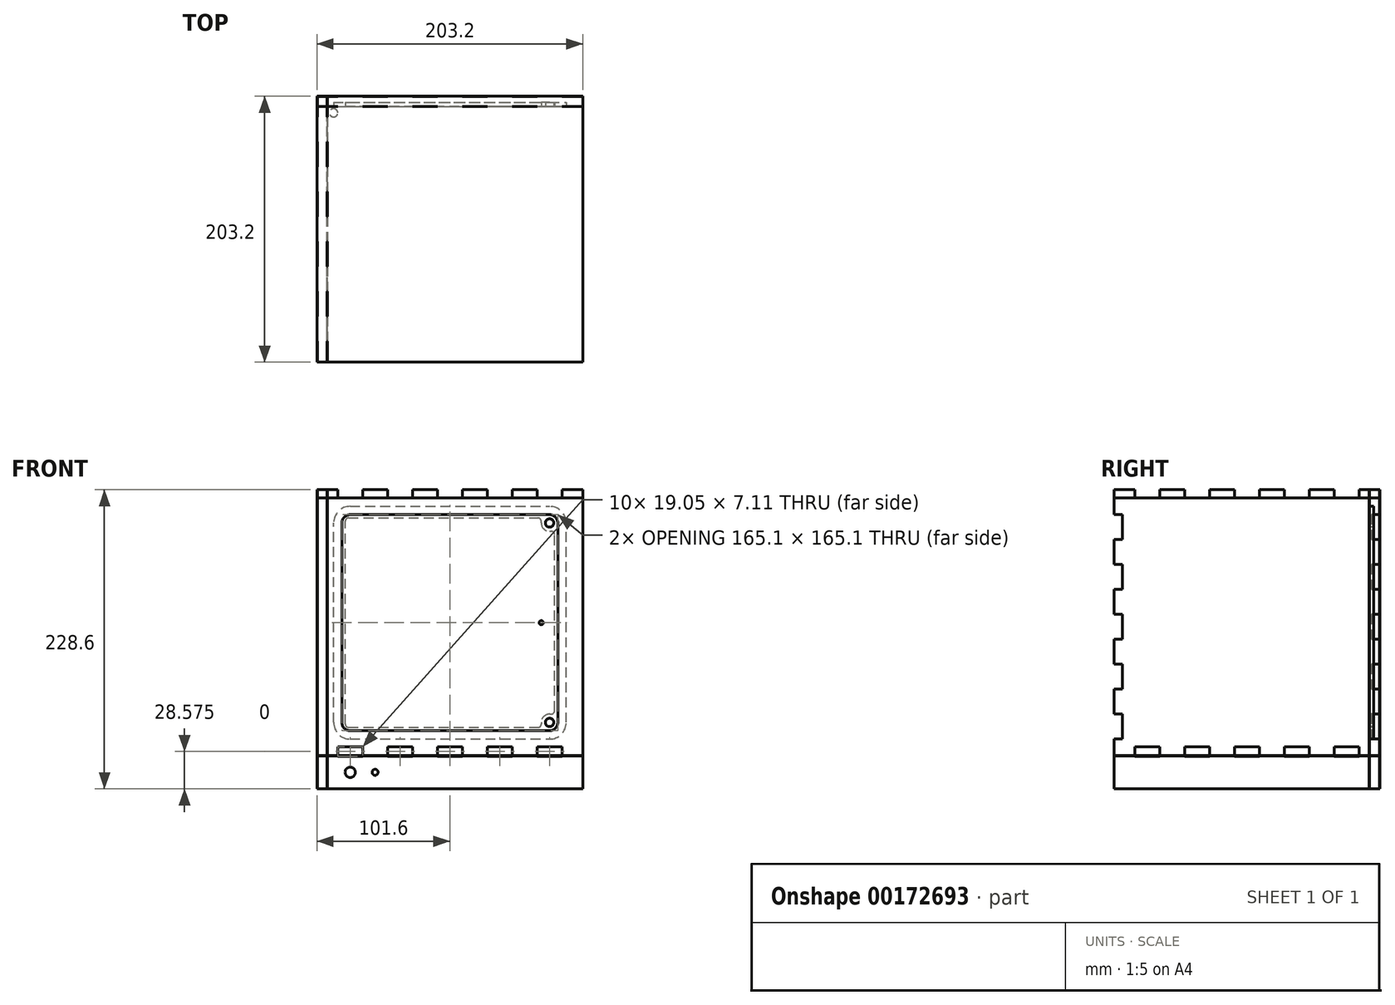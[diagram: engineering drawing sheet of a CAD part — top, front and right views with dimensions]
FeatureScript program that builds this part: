
annotation { "Feature Type Name" : "Feature", "Feature Type Description" : "" }
export const myFeature = defineFeature(function(context is Context, id is Id, definition is map)
    precondition{}
    {
        {
            assignVariable(context, id + "F0", {"name" : "thick", "anyValue" : 0.25});
        }
        {
            assignVariable(context, id + "F1", {"name" : "kerf", "anyValue" : .15});
        }
        {
            var Q0;
            Q0=qCreatedBy(makeId("Right.planeOp"),FACE);
            var sketch = newSketch(context, id + "F2", { "sketchPlane" : qUnion([Q0])});
            skLineSegment(sketch, "E0.bottom", {"start": v(-101.6, -114.3) * mm, "end": v(101.6, -114.3) * mm});
            skLineSegment(sketch, "E0.top", {"start": v(-101.6, 114.3) * mm, "end": v(101.6, 114.3) * mm});
            skLineSegment(sketch, "E0.left", {"start": v(-101.6, -114.3) * mm, "end": v(-101.6, 114.3) * mm});
            skLineSegment(sketch, "E0.right", {"start": v(101.6, -114.3) * mm, "end": v(101.6, 114.3) * mm});
            skPoint(sketch, "E0.middle", {"position": v(0, 0) * mm});
            skSolve(sketch);
        }
        {
            var Q0;
            Q0 = qSketchRegion(id + "F2", true);
            extrude(context, id + "F3", {"entities" : qUnion([Q0]), "depth" : (getVariable(context, 'thick')) * mm});
        }
        {
            var Q0;
            Q0=makeQuery(id+"F3.opExtrude","CAP_FACE",FACE,{"disambiguationData":[OSD([sQuery(id+"F2.wireOp",EDGE,"E0.bottom"),sQuery(id+"F2.wireOp",EDGE,"E0.top"),sQuery(id+"F2.wireOp",EDGE,"E0.left"),sQuery(id+"F2.wireOp",EDGE,"E0.right")])],"isStart":true});
            var sketch = newSketch(context, id + "F4", { "sketchPlane" : qUnion([Q0])});
            skLineSegment(sketch, "E1.bottom", {"start": v(9.52, 107.95) * mm, "end": v(-9.53, 107.95) * mm});
            skLineSegment(sketch, "E1.top", {"start": v(9.52, 114.3) * mm, "end": v(-9.53, 114.3) * mm});
            skLineSegment(sketch, "E1.left", {"start": v(9.52, 107.95) * mm, "end": v(9.52, 114.3) * mm});
            skLineSegment(sketch, "E1.right", {"start": v(-9.53, 107.95) * mm, "end": v(-9.53, 114.3) * mm});
            skPoint(sketch, "E1.middle", {"position": v(0, 111.13) * mm});
            skLineSegment(sketch, "E2.1.0.0", {"start": v(47.62, 114.3) * mm, "end": v(28.57, 114.3) * mm});
            skLineSegment(sketch, "E2.1.0.1", {"start": v(47.62, 107.95) * mm, "end": v(28.57, 107.95) * mm});
            skPoint(sketch, "E2.1.0.2", {"position": v(38.1, 111.13) * mm});
            skLineSegment(sketch, "E2.1.0.3", {"start": v(28.57, 107.95) * mm, "end": v(28.57, 114.3) * mm});
            skLineSegment(sketch, "E2.1.0.4", {"start": v(47.62, 107.95) * mm, "end": v(47.62, 114.3) * mm});
            skLineSegment(sketch, "E2.2.0.0", {"start": v(85.72, 114.3) * mm, "end": v(66.67, 114.3) * mm});
            skLineSegment(sketch, "E2.2.0.1", {"start": v(85.72, 107.95) * mm, "end": v(66.67, 107.95) * mm});
            skPoint(sketch, "E2.2.0.2", {"position": v(76.2, 111.13) * mm});
            skLineSegment(sketch, "E2.2.0.3", {"start": v(66.67, 107.95) * mm, "end": v(66.67, 114.3) * mm});
            skLineSegment(sketch, "E2.2.0.4", {"start": v(85.72, 107.95) * mm, "end": v(85.72, 114.3) * mm});
            skLineSegment(sketch, "E2.direction1", {"start": v(-9.53, 107.95) * mm, "end": v(28.57, 107.95) * mm, "construction": true});
            skPoint(sketch, "E3.1.0.0", {"position": v(-38.1, 111.13) * mm});
            skLineSegment(sketch, "E3.1.0.1", {"start": v(-28.58, 107.95) * mm, "end": v(-47.63, 107.95) * mm});
            skLineSegment(sketch, "E3.1.0.2", {"start": v(-28.58, 114.3) * mm, "end": v(-47.63, 114.3) * mm});
            skLineSegment(sketch, "E3.1.0.3", {"start": v(-28.58, 107.95) * mm, "end": v(-28.58, 114.3) * mm});
            skLineSegment(sketch, "E3.1.0.4", {"start": v(-47.63, 107.95) * mm, "end": v(-47.63, 114.3) * mm});
            skPoint(sketch, "E3.2.0.0", {"position": v(-76.2, 111.13) * mm});
            skLineSegment(sketch, "E3.2.0.1", {"start": v(-66.68, 107.95) * mm, "end": v(-85.73, 107.95) * mm});
            skLineSegment(sketch, "E3.2.0.2", {"start": v(-66.68, 114.3) * mm, "end": v(-85.73, 114.3) * mm});
            skLineSegment(sketch, "E3.2.0.3", {"start": v(-66.68, 107.95) * mm, "end": v(-66.68, 114.3) * mm});
            skLineSegment(sketch, "E3.2.0.4", {"start": v(-85.73, 107.95) * mm, "end": v(-85.73, 114.3) * mm});
            skLineSegment(sketch, "E3.direction1", {"start": v(-9.53, 107.95) * mm, "end": v(-47.63, 107.95) * mm, "construction": true});
            skLineSegment(sketch, "E4.bottom", {"start": v(-95.25, 0) * mm, "end": v(-101.6, 0) * mm});
            skLineSegment(sketch, "E4.top", {"start": v(-95.25, 19.05) * mm, "end": v(-101.6, 19.05) * mm});
            skLineSegment(sketch, "E4.left", {"start": v(-95.25, 0) * mm, "end": v(-95.25, 19.05) * mm});
            skLineSegment(sketch, "E4.right", {"start": v(-101.6, 0) * mm, "end": v(-101.6, 19.05) * mm});
            skPoint(sketch, "E4.middle", {"position": v(-98.42, 9.52) * mm});
            skPoint(sketch, "E4.centerSnap0", {"position": v(-101.6, 9.52) * mm});
            skPoint(sketch, "E5.0.1.0", {"position": v(-101.6, 47.63) * mm});
            skLineSegment(sketch, "E5.0.1.1", {"start": v(-95.25, 38.1) * mm, "end": v(-95.25, 57.15) * mm});
            skPoint(sketch, "E5.0.1.2", {"position": v(-98.42, 47.63) * mm});
            skLineSegment(sketch, "E5.0.1.3", {"start": v(-95.25, 38.1) * mm, "end": v(-101.6, 38.1) * mm});
            skLineSegment(sketch, "E5.0.1.4", {"start": v(-95.25, 57.15) * mm, "end": v(-101.6, 57.15) * mm});
            skLineSegment(sketch, "E5.0.1.5", {"start": v(-101.6, 38.1) * mm, "end": v(-101.6, 57.15) * mm});
            skPoint(sketch, "E5.0.2.0", {"position": v(-101.6, 85.73) * mm});
            skLineSegment(sketch, "E5.0.2.1", {"start": v(-95.25, 76.2) * mm, "end": v(-95.25, 95.25) * mm});
            skPoint(sketch, "E5.0.2.2", {"position": v(-98.42, 85.73) * mm});
            skLineSegment(sketch, "E5.0.2.3", {"start": v(-95.25, 76.2) * mm, "end": v(-101.6, 76.2) * mm});
            skLineSegment(sketch, "E5.0.2.4", {"start": v(-95.25, 95.25) * mm, "end": v(-101.6, 95.25) * mm});
            skLineSegment(sketch, "E5.0.2.5", {"start": v(-101.6, 76.2) * mm, "end": v(-101.6, 95.25) * mm});
            skLineSegment(sketch, "E5.direction1", {"start": v(-101.6, 0) * mm, "end": v(-76.2, 0) * mm, "construction": true});
            skLineSegment(sketch, "E5.direction2", {"start": v(-101.6, 0) * mm, "end": v(-101.6, 38.1) * mm, "construction": true});
            skPoint(sketch, "E6.0.1.0", {"position": v(-101.6, -28.58) * mm});
            skLineSegment(sketch, "E6.0.1.1", {"start": v(-101.6, -38.1) * mm, "end": v(-101.6, -19.05) * mm});
            skPoint(sketch, "E6.0.1.2", {"position": v(-98.42, -28.58) * mm});
            skLineSegment(sketch, "E6.0.1.3", {"start": v(-95.25, -38.1) * mm, "end": v(-95.25, -19.05) * mm});
            skLineSegment(sketch, "E6.0.1.4", {"start": v(-95.25, -19.05) * mm, "end": v(-101.6, -19.05) * mm});
            skLineSegment(sketch, "E6.0.1.5", {"start": v(-95.25, -38.1) * mm, "end": v(-101.6, -38.1) * mm});
            skPoint(sketch, "E6.0.2.0", {"position": v(-101.6, -66.68) * mm});
            skLineSegment(sketch, "E6.0.2.1", {"start": v(-101.6, -76.2) * mm, "end": v(-101.6, -57.15) * mm});
            skPoint(sketch, "E6.0.2.2", {"position": v(-98.42, -66.68) * mm});
            skLineSegment(sketch, "E6.0.2.3", {"start": v(-95.25, -76.2) * mm, "end": v(-95.25, -57.15) * mm});
            skLineSegment(sketch, "E6.0.2.4", {"start": v(-95.25, -57.15) * mm, "end": v(-101.6, -57.15) * mm});
            skLineSegment(sketch, "E6.0.2.5", {"start": v(-95.25, -76.2) * mm, "end": v(-101.6, -76.2) * mm});
            skLineSegment(sketch, "E6.direction2", {"start": v(-101.6, 0) * mm, "end": v(-101.6, -38.1) * mm, "construction": true});
            skLineSegment(sketch, "E7", {"start": v(0, 114.3) * mm, "end": v(0, -114.3) * mm, "construction": true});
            skLineSegment(sketch, "E8.MirrorCS", {"start": v(95.25, -76.2) * mm, "end": v(101.6, -76.2) * mm});
            skLineSegment(sketch, "E9.MirrorCS", {"start": v(95.25, 38.1) * mm, "end": v(101.6, 38.1) * mm});
            skLineSegment(sketch, "E10.MirrorCS", {"start": v(95.25, 19.05) * mm, "end": v(101.6, 19.05) * mm});
            skLineSegment(sketch, "E11.MirrorCS", {"start": v(95.25, -38.1) * mm, "end": v(101.6, -38.1) * mm});
            skLineSegment(sketch, "E12.MirrorCS", {"start": v(95.25, 95.25) * mm, "end": v(101.6, 95.25) * mm});
            skLineSegment(sketch, "E13.MirrorCS", {"start": v(95.25, -57.15) * mm, "end": v(101.6, -57.15) * mm});
            skLineSegment(sketch, "E14.MirrorCS", {"start": v(95.25, 0) * mm, "end": v(101.6, 0) * mm});
            skLineSegment(sketch, "E15.MirrorCS", {"start": v(95.25, -19.05) * mm, "end": v(101.6, -19.05) * mm});
            skLineSegment(sketch, "E16.MirrorCS", {"start": v(95.25, 76.2) * mm, "end": v(101.6, 76.2) * mm});
            skLineSegment(sketch, "E17.MirrorCS", {"start": v(95.25, 57.15) * mm, "end": v(101.6, 57.15) * mm});
            skLineSegment(sketch, "E18.MirrorCS", {"start": v(101.6, -38.1) * mm, "end": v(101.6, -19.05) * mm});
            skLineSegment(sketch, "E19.MirrorCS", {"start": v(101.6, 0) * mm, "end": v(101.6, 19.05) * mm});
            skPoint(sketch, "E20.MirrorP", {"position": v(101.6, 9.53) * mm});
            skPoint(sketch, "E21.MirrorP", {"position": v(101.6, 85.73) * mm});
            skLineSegment(sketch, "E22.MirrorCS", {"start": v(101.6, 38.1) * mm, "end": v(101.6, 57.15) * mm});
            skPoint(sketch, "E23.MirrorP", {"position": v(101.6, -66.67) * mm});
            skLineSegment(sketch, "E24.MirrorCS", {"start": v(101.6, 0) * mm, "end": v(101.6, 38.1) * mm, "construction": true});
            skLineSegment(sketch, "E25.MirrorCS", {"start": v(101.6, 0) * mm, "end": v(101.6, -38.1) * mm, "construction": true});
            skPoint(sketch, "E26.MirrorP", {"position": v(98.43, -28.57) * mm});
            skLineSegment(sketch, "E27.MirrorCS", {"start": v(95.25, 38.1) * mm, "end": v(95.25, 57.15) * mm});
            skPoint(sketch, "E28.MirrorP", {"position": v(98.43, 9.53) * mm});
            skPoint(sketch, "E29.MirrorP", {"position": v(101.6, -28.57) * mm});
            skPoint(sketch, "E30.MirrorP", {"position": v(98.42, 85.73) * mm});
            skLineSegment(sketch, "E31.MirrorCS", {"start": v(101.6, 76.2) * mm, "end": v(101.6, 95.25) * mm});
            skPoint(sketch, "E32.MirrorP", {"position": v(98.43, 47.63) * mm});
            skPoint(sketch, "E33.MirrorP", {"position": v(101.6, 47.63) * mm});
            skPoint(sketch, "E34.MirrorP", {"position": v(98.43, -66.67) * mm});
            skLineSegment(sketch, "E35.MirrorCS", {"start": v(95.25, 76.2) * mm, "end": v(95.25, 95.25) * mm});
            skLineSegment(sketch, "E36.MirrorCS", {"start": v(95.25, -38.1) * mm, "end": v(95.25, -19.05) * mm});
            skLineSegment(sketch, "E37.MirrorCS", {"start": v(95.25, -76.2) * mm, "end": v(95.25, -57.15) * mm});
            skLineSegment(sketch, "E38.MirrorCS", {"start": v(95.25, 0) * mm, "end": v(95.25, 19.05) * mm});
            skLineSegment(sketch, "E39.MirrorCS", {"start": v(101.6, -76.2) * mm, "end": v(101.6, -57.15) * mm});
            skLineSegment(sketch, "E40", {"start": v(-101.6, -88.9) * mm, "end": v(101.6, -88.9) * mm, "construction": true});
            skLineSegment(sketch, "E41.bottom", {"start": v(9.52, -89.28) * mm, "end": v(-9.53, -89.28) * mm});
            skLineSegment(sketch, "E41.top", {"start": v(9.52, -82.17) * mm, "end": v(-9.53, -82.17) * mm});
            skLineSegment(sketch, "E41.left", {"start": v(9.52, -89.28) * mm, "end": v(9.52, -82.17) * mm});
            skLineSegment(sketch, "E41.right", {"start": v(-9.53, -89.28) * mm, "end": v(-9.53, -82.17) * mm});
            skPoint(sketch, "E41.middle", {"position": v(0, -85.73) * mm});
            skLineSegment(sketch, "E42.1.0.0", {"start": v(47.62, -89.28) * mm, "end": v(47.62, -82.17) * mm});
            skLineSegment(sketch, "E42.1.0.1", {"start": v(28.57, -89.28) * mm, "end": v(28.57, -82.17) * mm});
            skPoint(sketch, "E42.1.0.2", {"position": v(38.1, -85.73) * mm});
            skLineSegment(sketch, "E42.1.0.3", {"start": v(47.62, -82.17) * mm, "end": v(28.57, -82.17) * mm});
            skLineSegment(sketch, "E42.1.0.4", {"start": v(47.62, -89.28) * mm, "end": v(28.57, -89.28) * mm});
            skLineSegment(sketch, "E42.2.0.0", {"start": v(85.72, -89.28) * mm, "end": v(85.72, -82.17) * mm});
            skLineSegment(sketch, "E42.2.0.1", {"start": v(66.67, -89.28) * mm, "end": v(66.67, -82.17) * mm});
            skPoint(sketch, "E42.2.0.2", {"position": v(76.2, -85.73) * mm});
            skLineSegment(sketch, "E42.2.0.3", {"start": v(85.72, -82.17) * mm, "end": v(66.67, -82.17) * mm});
            skLineSegment(sketch, "E42.2.0.4", {"start": v(85.72, -89.28) * mm, "end": v(66.67, -89.28) * mm});
            skLineSegment(sketch, "E42.direction1", {"start": v(-9.53, -89.28) * mm, "end": v(28.57, -89.28) * mm, "construction": true});
            skLineSegment(sketch, "E43.MirrorCS", {"start": v(-28.58, -89.28) * mm, "end": v(-28.57, -82.17) * mm});
            skLineSegment(sketch, "E44.MirrorCS", {"start": v(-47.63, -89.28) * mm, "end": v(-28.58, -89.28) * mm});
            skLineSegment(sketch, "E45.MirrorCS", {"start": v(-47.63, -82.17) * mm, "end": v(-28.58, -82.17) * mm});
            skLineSegment(sketch, "E46.MirrorCS", {"start": v(-85.73, -89.28) * mm, "end": v(-85.73, -82.17) * mm});
            skLineSegment(sketch, "E47.MirrorCS", {"start": v(-66.67, -89.28) * mm, "end": v(-66.67, -82.17) * mm});
            skLineSegment(sketch, "E48.MirrorCS", {"start": v(-85.73, -82.17) * mm, "end": v(-66.68, -82.17) * mm});
            skPoint(sketch, "E49.MirrorP", {"position": v(-38.1, -85.73) * mm});
            skPoint(sketch, "E50.MirrorP", {"position": v(-76.2, -85.73) * mm});
            skLineSegment(sketch, "E51.MirrorCS", {"start": v(-47.63, -89.28) * mm, "end": v(-47.63, -82.17) * mm});
            skLineSegment(sketch, "E52.MirrorCS", {"start": v(-85.73, -89.28) * mm, "end": v(-66.67, -89.28) * mm});
            skSolve(sketch);
        }
        {
            var Q0;
            Q0 = qSketchRegion(id + "F4", true);
            extrude(context, id + "F5", {"entities" : qUnion([Q0]), "operationType" : NewBodyOperationType.REMOVE, "endBound" : BoundingType.THROUGH_ALL, "oppositeDirection" : true, "depth" : 25.4 * mm});
        }
        {
            var Q0;
            Q0=makeQuery(id+"F3.opExtrude","SWEPT_BODY",BODY,{"disambiguationData":[OSD([sQuery(id+"F2.wireOp",EDGE,"E0.bottom"),sQuery(id+"F2.wireOp",EDGE,"E0.top"),sQuery(id+"F2.wireOp",EDGE,"E0.left"),sQuery(id+"F2.wireOp",EDGE,"E0.right")])]});
            var Q1;
            Q1=makeQuery(id+"F3.opExtrude","SWEPT_EDGE",EDGE,{"disambiguationData":[OSD([sQuery(id+"F2.wireOp",EDGE,"E0.bottom"),sQuery(id+"F2.wireOp",EDGE,"E0.left")])]});
            transform(context, id + "F6", {"entities" : qUnion([Q0]), "transformType" : TransformType.TRANSLATION_DISTANCE, "transformDirection" : qUnion([Q1]), "distance" : (8 - getVariable(context, 'thick')) * mm, "oppositeDirection" : true, "makeCopy" : true});
        }
        {
            var Q0;
            {var subQ0=sQuery(id+"F2.wireOp",EDGE,"E0.bottom");var subQ1=sQuery(id+"F2.wireOp",EDGE,"E0.right");Q0=makeQuery(id+"F5.boolean.opBoolean","SPLIT",FACE,{"disambiguationData":[TD([makeQuery(id+"F3.opExtrude","SWEPT_FACE",FACE,{"disambiguationData":[OSD([subQ0])]})])],"derivedFrom":makeQuery(id+"F3.opExtrude","SWEPT_FACE",FACE,{"disambiguationData":[OSD([subQ1])]})});}
            var sketch = newSketch(context, id + "F7", { "sketchPlane" : qUnion([Q0])});
            skLineSegment(sketch, "E53.bottom", {"start": v(0, -114.3) * mm, "end": v(-203.2, -114.3) * mm});
            skLineSegment(sketch, "E53.top", {"start": v(0, 114.3) * mm, "end": v(-203.2, 114.3) * mm});
            skLineSegment(sketch, "E53.left", {"start": v(0, -114.3) * mm, "end": v(0, 114.3) * mm});
            skLineSegment(sketch, "E53.right", {"start": v(-203.2, -114.3) * mm, "end": v(-203.2, 114.3) * mm});
            skSolve(sketch);
        }
        {
            var Q0;
            Q0 = qSketchRegion(id + "F7", true);
            extrude(context, id + "F8", {"entities" : qUnion([Q0]), "oppositeDirection" : true, "depth" : (getVariable(context, 'thick')) * mm});
        }
        {
            var Q0;
            Q0=makeQuery(id+"F3.opExtrude","SWEPT_BODY",BODY,{"disambiguationData":[OSD([sQuery(id+"F2.wireOp",EDGE,"E0.bottom"),sQuery(id+"F2.wireOp",EDGE,"E0.top"),sQuery(id+"F2.wireOp",EDGE,"E0.left"),sQuery(id+"F2.wireOp",EDGE,"E0.right")])]});
            var Q1;
            Q1=makeQuery(id+"F6.opPattern","COPY",BODY,{"derivedFrom":makeQuery(id+"F3.opExtrude","SWEPT_BODY",BODY,{"disambiguationData":[OSD([sQuery(id+"F2.wireOp",EDGE,"E0.bottom"),sQuery(id+"F2.wireOp",EDGE,"E0.top"),sQuery(id+"F2.wireOp",EDGE,"E0.left"),sQuery(id+"F2.wireOp",EDGE,"E0.right")])]}),"instanceName":"1"});
            var Q2;
            Q2=makeQuery(id+"F8.opExtrude","SWEPT_BODY",BODY,{"disambiguationData":[OSD([sQuery(id+"F7.wireOp",EDGE,"E53.bottom"),sQuery(id+"F7.wireOp",EDGE,"E53.top"),sQuery(id+"F7.wireOp",EDGE,"E53.left"),sQuery(id+"F7.wireOp",EDGE,"E53.right")])]});
            booleanBodies(context, id + "F9", {"operationType" : BooleanOperationType.SUBTRACTION, "tools" : qUnion([Q0, Q1]), "targets" : qUnion([Q2]), "keepTools" : true});
        }
        {
            var Q0;
            Q0=makeQuery(id+"F8.opExtrude","CAP_FACE",FACE,{"disambiguationData":[OSD([sQuery(id+"F7.wireOp",EDGE,"E53.bottom"),sQuery(id+"F7.wireOp",EDGE,"E53.top"),sQuery(id+"F7.wireOp",EDGE,"E53.left"),sQuery(id+"F7.wireOp",EDGE,"E53.right")])],"isStart":true});
            var sketch = newSketch(context, id + "F10", { "sketchPlane" : qUnion([Q0])});
            skLineSegment(sketch, "E54", {"start": v(-203.2, -89.28) * mm, "end": v(0, -89.28) * mm, "construction": true});
            skLineSegment(sketch, "E55", {"start": v(-203.2, -82.17) * mm, "end": v(0, -82.17) * mm, "construction": true});
            skLineSegment(sketch, "E56", {"start": v(-101.6, 114.3) * mm, "end": v(-101.6, -114.3) * mm, "construction": true});
            skLineSegment(sketch, "E57.bottom", {"start": v(-92.07, -82.17) * mm, "end": v(-111.12, -82.17) * mm});
            skLineSegment(sketch, "E57.top", {"start": v(-92.07, -89.28) * mm, "end": v(-111.12, -89.28) * mm});
            skLineSegment(sketch, "E57.left", {"start": v(-92.07, -82.17) * mm, "end": v(-92.07, -89.28) * mm});
            skLineSegment(sketch, "E57.right", {"start": v(-111.12, -82.17) * mm, "end": v(-111.12, -89.28) * mm});
            skPoint(sketch, "E57.middle", {"position": v(-101.6, -85.73) * mm});
            skLineSegment(sketch, "E58.1.0.0", {"start": v(-73.02, -82.17) * mm, "end": v(-73.02, -89.28) * mm});
            skLineSegment(sketch, "E58.1.0.1", {"start": v(-53.97, -89.28) * mm, "end": v(-73.02, -89.28) * mm});
            skLineSegment(sketch, "E58.1.0.2", {"start": v(-53.97, -82.17) * mm, "end": v(-53.97, -89.28) * mm});
            skLineSegment(sketch, "E58.1.0.3", {"start": v(-53.97, -82.17) * mm, "end": v(-73.02, -82.17) * mm});
            skPoint(sketch, "E58.1.0.4", {"position": v(-63.5, -85.73) * mm});
            skLineSegment(sketch, "E58.2.0.0", {"start": v(-34.92, -82.17) * mm, "end": v(-34.92, -89.28) * mm});
            skLineSegment(sketch, "E58.2.0.1", {"start": v(-15.87, -89.28) * mm, "end": v(-34.92, -89.28) * mm});
            skLineSegment(sketch, "E58.2.0.2", {"start": v(-15.87, -82.17) * mm, "end": v(-15.87, -89.28) * mm});
            skLineSegment(sketch, "E58.2.0.3", {"start": v(-15.87, -82.17) * mm, "end": v(-34.92, -82.17) * mm});
            skPoint(sketch, "E58.2.0.4", {"position": v(-25.4, -85.73) * mm});
            skLineSegment(sketch, "E58.direction1", {"start": v(-111.12, -89.28) * mm, "end": v(-73.02, -89.28) * mm, "construction": true});
            skLineSegment(sketch, "E59.MirrorCS", {"start": v(-187.33, -82.17) * mm, "end": v(-168.28, -82.17) * mm});
            skLineSegment(sketch, "E60.MirrorCS", {"start": v(-187.33, -82.17) * mm, "end": v(-187.33, -89.28) * mm});
            skPoint(sketch, "E61.MirrorP", {"position": v(-177.8, -85.73) * mm});
            skPoint(sketch, "E62.MirrorP", {"position": v(-139.7, -85.73) * mm});
            skLineSegment(sketch, "E63.MirrorCS", {"start": v(-187.33, -89.28) * mm, "end": v(-168.28, -89.28) * mm});
            skLineSegment(sketch, "E64.MirrorCS", {"start": v(-168.28, -82.17) * mm, "end": v(-168.28, -89.28) * mm});
            skLineSegment(sketch, "E65.MirrorCS", {"start": v(-149.23, -82.17) * mm, "end": v(-130.18, -82.17) * mm});
            skLineSegment(sketch, "E66.MirrorCS", {"start": v(-149.23, -82.17) * mm, "end": v(-149.23, -89.28) * mm});
            skLineSegment(sketch, "E67.MirrorCS", {"start": v(-130.18, -82.17) * mm, "end": v(-130.18, -89.28) * mm});
            skLineSegment(sketch, "E68.MirrorCS", {"start": v(-149.23, -89.28) * mm, "end": v(-130.18, -89.28) * mm});
            skLineSegment(sketch, "E69.bottom", {"start": v(-92.07, 114.3) * mm, "end": v(-111.12, 114.3) * mm});
            skLineSegment(sketch, "E69.top", {"start": v(-92.07, 107.95) * mm, "end": v(-111.12, 107.95) * mm});
            skLineSegment(sketch, "E69.left", {"start": v(-92.07, 114.3) * mm, "end": v(-92.07, 107.95) * mm});
            skLineSegment(sketch, "E69.right", {"start": v(-111.12, 114.3) * mm, "end": v(-111.12, 107.95) * mm});
            skPoint(sketch, "E69.middle", {"position": v(-101.6, 111.13) * mm});
            skLineSegment(sketch, "E70.1.0.0", {"start": v(-53.97, 114.3) * mm, "end": v(-73.02, 114.3) * mm});
            skLineSegment(sketch, "E70.1.0.1", {"start": v(-53.97, 107.95) * mm, "end": v(-73.02, 107.95) * mm});
            skLineSegment(sketch, "E70.1.0.2", {"start": v(-53.97, 114.3) * mm, "end": v(-53.97, 107.95) * mm});
            skPoint(sketch, "E70.1.0.3", {"position": v(-63.5, 111.13) * mm});
            skLineSegment(sketch, "E70.1.0.4", {"start": v(-73.02, 114.3) * mm, "end": v(-73.02, 107.95) * mm});
            skLineSegment(sketch, "E70.2.0.0", {"start": v(-15.87, 114.3) * mm, "end": v(-34.92, 114.3) * mm});
            skLineSegment(sketch, "E70.2.0.1", {"start": v(-15.87, 107.95) * mm, "end": v(-34.92, 107.95) * mm});
            skLineSegment(sketch, "E70.2.0.2", {"start": v(-15.87, 114.3) * mm, "end": v(-15.87, 107.95) * mm});
            skPoint(sketch, "E70.2.0.3", {"position": v(-25.4, 111.13) * mm});
            skLineSegment(sketch, "E70.2.0.4", {"start": v(-34.92, 114.3) * mm, "end": v(-34.92, 107.95) * mm});
            skLineSegment(sketch, "E70.direction1", {"start": v(-111.12, 107.95) * mm, "end": v(-73.02, 107.95) * mm, "construction": true});
            skLineSegment(sketch, "E71.MirrorCS", {"start": v(-149.23, 107.95) * mm, "end": v(-130.18, 107.95) * mm});
            skPoint(sketch, "E72.MirrorP", {"position": v(-139.7, 111.13) * mm});
            skLineSegment(sketch, "E73.MirrorCS", {"start": v(-187.33, 114.3) * mm, "end": v(-168.28, 114.3) * mm});
            skLineSegment(sketch, "E74.MirrorCS", {"start": v(-168.28, 114.3) * mm, "end": v(-168.28, 107.95) * mm});
            skLineSegment(sketch, "E75.MirrorCS", {"start": v(-130.18, 114.3) * mm, "end": v(-130.18, 107.95) * mm});
            skLineSegment(sketch, "E76.MirrorCS", {"start": v(-187.33, 114.3) * mm, "end": v(-187.33, 107.95) * mm});
            skLineSegment(sketch, "E77.MirrorCS", {"start": v(-187.33, 107.95) * mm, "end": v(-168.28, 107.95) * mm});
            skLineSegment(sketch, "E78.MirrorCS", {"start": v(-149.23, 114.3) * mm, "end": v(-149.23, 107.95) * mm});
            skLineSegment(sketch, "E79.MirrorCS", {"start": v(-149.23, 114.3) * mm, "end": v(-130.18, 114.3) * mm});
            skPoint(sketch, "E80.MirrorP", {"position": v(-177.8, 111.13) * mm});
            skSolve(sketch);
        }
        {
            var Q0;
            Q0 = qSketchRegion(id + "F10", true);
            extrude(context, id + "F11", {"entities" : qUnion([Q0]), "operationType" : NewBodyOperationType.REMOVE, "endBound" : BoundingType.THROUGH_ALL, "oppositeDirection" : true, "depth" : 25.4 * mm});
        }
        {
            var Q0;
            Q0=makeQuery(id+"F8.opExtrude","SWEPT_BODY",BODY,{"disambiguationData":[OSD([sQuery(id+"F7.wireOp",EDGE,"E53.bottom"),sQuery(id+"F7.wireOp",EDGE,"E53.top"),sQuery(id+"F7.wireOp",EDGE,"E53.left"),sQuery(id+"F7.wireOp",EDGE,"E53.right")])]});
            var Q1;
            Q1=makeQuery(id+"F3.opExtrude","CAP_EDGE",EDGE,{"disambiguationData":[OSD([sQuery(id+"F2.wireOp",EDGE,"E0.bottom")])],"isStart":true});
            transform(context, id + "F12", {"entities" : qUnion([Q0]), "transformType" : TransformType.TRANSLATION_DISTANCE, "transformDirection" : qUnion([Q1]), "distance" : (8 - getVariable(context, 'thick')) * mm, "oppositeDirection" : true, "makeCopy" : true});
        }
        {
            var Q0;
            Q0=makeQuery(id+"F6.opPattern","COPY",FACE,{"derivedFrom":makeQuery(id+"F5.boolean.opBoolean","COPY",FACE,{"derivedFrom":makeQuery(id+"F5.opExtrude","SWEPT_FACE",FACE,{"disambiguationData":[OSD([sQuery(id+"F4.wireOp",EDGE,"E3.2.0.1")])]})}),"instanceName":"1"});
            var sketch = newSketch(context, id + "F13", { "sketchPlane" : qUnion([Q0])});
            skLineSegment(sketch, "E81.bottom", {"start": v(203.2, 101.6) * mm, "end": v(0, 101.6) * mm});
            skLineSegment(sketch, "E81.top", {"start": v(203.2, -101.6) * mm, "end": v(0, -101.6) * mm});
            skLineSegment(sketch, "E81.left", {"start": v(203.2, 101.6) * mm, "end": v(203.2, -101.6) * mm});
            skLineSegment(sketch, "E81.right", {"start": v(0, 101.6) * mm, "end": v(0, -101.6) * mm});
            skSolve(sketch);
        }
        {
            var Q0;
            Q0 = qSketchRegion(id + "F13", true);
            extrude(context, id + "F14", {"entities" : qUnion([Q0]), "depth" : (getVariable(context, 'thick')) * mm});
        }
        {
            var Q0;
            Q0=makeQuery(id+"F3.opExtrude","SWEPT_BODY",BODY,{"disambiguationData":[OSD([sQuery(id+"F2.wireOp",EDGE,"E0.bottom"),sQuery(id+"F2.wireOp",EDGE,"E0.top"),sQuery(id+"F2.wireOp",EDGE,"E0.left"),sQuery(id+"F2.wireOp",EDGE,"E0.right")])]});
            var Q1;
            Q1=makeQuery(id+"F6.opPattern","COPY",BODY,{"derivedFrom":makeQuery(id+"F3.opExtrude","SWEPT_BODY",BODY,{"disambiguationData":[OSD([sQuery(id+"F2.wireOp",EDGE,"E0.bottom"),sQuery(id+"F2.wireOp",EDGE,"E0.top"),sQuery(id+"F2.wireOp",EDGE,"E0.left"),sQuery(id+"F2.wireOp",EDGE,"E0.right")])]}),"instanceName":"1"});
            var Q2;
            Q2=makeQuery(id+"F8.opExtrude","SWEPT_BODY",BODY,{"disambiguationData":[OSD([sQuery(id+"F7.wireOp",EDGE,"E53.bottom"),sQuery(id+"F7.wireOp",EDGE,"E53.top"),sQuery(id+"F7.wireOp",EDGE,"E53.left"),sQuery(id+"F7.wireOp",EDGE,"E53.right")])]});
            var Q3;
            Q3=makeQuery(id+"F12.opPattern","COPY",BODY,{"derivedFrom":makeQuery(id+"F8.opExtrude","SWEPT_BODY",BODY,{"disambiguationData":[OSD([sQuery(id+"F7.wireOp",EDGE,"E53.bottom"),sQuery(id+"F7.wireOp",EDGE,"E53.top"),sQuery(id+"F7.wireOp",EDGE,"E53.left"),sQuery(id+"F7.wireOp",EDGE,"E53.right")])]}),"instanceName":"1"});
            var Q4;
            Q4=makeQuery(id+"F14.opExtrude","SWEPT_BODY",BODY,{"disambiguationData":[OSD([sQuery(id+"F13.wireOp",EDGE,"E81.bottom"),sQuery(id+"F13.wireOp",EDGE,"E81.top"),sQuery(id+"F13.wireOp",EDGE,"E81.left"),sQuery(id+"F13.wireOp",EDGE,"E81.right")])]});
            booleanBodies(context, id + "F15", {"operationType" : BooleanOperationType.SUBTRACTION, "tools" : qUnion([Q0, Q1, Q2, Q3]), "targets" : qUnion([Q4]), "keepTools" : true});
        }
        {
            var Q0;
            Q0=makeQuery(id+"F12.opPattern","COPY",FACE,{"derivedFrom":makeQuery(id+"F11.boolean.opBoolean","COPY",FACE,{"derivedFrom":makeQuery(id+"F11.opExtrude","SWEPT_FACE",FACE,{"disambiguationData":[OSD([sQuery(id+"F10.wireOp",EDGE,"E58.1.0.1")])]})}),"instanceName":"1"});
            cPlane(context, id + "F16", {"entities" : qUnion([Q0]), "cplaneType" : CPlaneType.OFFSET, "offset" : (getVariable(context, 'kerf')) * mm, "width" : 152.4 * mm, "height" : 152.4 * mm});
        }
        {
            var Q0;
            Q0=qCreatedBy(id+"F16.planeOp",FACE);
            var sketch = newSketch(context, id + "F17", { "sketchPlane" : qUnion([Q0])});
            skLineSegment(sketch, "E82.bottom", {"start": v(203.2, -101.6) * mm, "end": v(0, -101.6) * mm});
            skLineSegment(sketch, "E82.top", {"start": v(203.2, 101.6) * mm, "end": v(0, 101.6) * mm});
            skLineSegment(sketch, "E82.left", {"start": v(203.2, -101.6) * mm, "end": v(203.2, 101.6) * mm});
            skLineSegment(sketch, "E82.right", {"start": v(0, -101.6) * mm, "end": v(0, 101.6) * mm});
            skSolve(sketch);
        }
        {
            var Q0;
            Q0 = qSketchRegion(id + "F17", true);
            extrude(context, id + "F18", {"entities" : qUnion([Q0]), "depth" : (getVariable(context, 'thick')) * mm});
        }
        {
            var Q0;
            Q0=makeQuery(id+"F3.opExtrude","SWEPT_BODY",BODY,{"disambiguationData":[OSD([sQuery(id+"F2.wireOp",EDGE,"E0.bottom"),sQuery(id+"F2.wireOp",EDGE,"E0.top"),sQuery(id+"F2.wireOp",EDGE,"E0.left"),sQuery(id+"F2.wireOp",EDGE,"E0.right")])]});
            var Q1;
            Q1=makeQuery(id+"F8.opExtrude","SWEPT_BODY",BODY,{"disambiguationData":[OSD([sQuery(id+"F7.wireOp",EDGE,"E53.bottom"),sQuery(id+"F7.wireOp",EDGE,"E53.top"),sQuery(id+"F7.wireOp",EDGE,"E53.left"),sQuery(id+"F7.wireOp",EDGE,"E53.right")])]});
            var Q2;
            Q2=makeQuery(id+"F6.opPattern","COPY",BODY,{"derivedFrom":makeQuery(id+"F3.opExtrude","SWEPT_BODY",BODY,{"disambiguationData":[OSD([sQuery(id+"F2.wireOp",EDGE,"E0.bottom"),sQuery(id+"F2.wireOp",EDGE,"E0.top"),sQuery(id+"F2.wireOp",EDGE,"E0.left"),sQuery(id+"F2.wireOp",EDGE,"E0.right")])]}),"instanceName":"1"});
            var Q3;
            Q3=makeQuery(id+"F12.opPattern","COPY",BODY,{"derivedFrom":makeQuery(id+"F8.opExtrude","SWEPT_BODY",BODY,{"disambiguationData":[OSD([sQuery(id+"F7.wireOp",EDGE,"E53.bottom"),sQuery(id+"F7.wireOp",EDGE,"E53.top"),sQuery(id+"F7.wireOp",EDGE,"E53.left"),sQuery(id+"F7.wireOp",EDGE,"E53.right")])]}),"instanceName":"1"});
            var Q4;
            Q4=makeQuery(id+"F18.opExtrude","SWEPT_BODY",BODY,{"disambiguationData":[OSD([sQuery(id+"F17.wireOp",EDGE,"E82.bottom"),sQuery(id+"F17.wireOp",EDGE,"E82.top"),sQuery(id+"F17.wireOp",EDGE,"E82.left"),sQuery(id+"F17.wireOp",EDGE,"E82.right")])]});
            booleanBodies(context, id + "F19", {"operationType" : BooleanOperationType.SUBTRACTION, "tools" : qUnion([Q0, Q1, Q2, Q3]), "targets" : qUnion([Q4]), "keepTools" : true});
        }
        {
            var Q0;
            Q0=makeQuery(id+"F12.opPattern","COPY",FACE,{"derivedFrom":makeQuery(id+"F8.opExtrude","CAP_FACE",FACE,{"disambiguationData":[OSD([sQuery(id+"F7.wireOp",EDGE,"E53.bottom"),sQuery(id+"F7.wireOp",EDGE,"E53.top"),sQuery(id+"F7.wireOp",EDGE,"E53.left"),sQuery(id+"F7.wireOp",EDGE,"E53.right")])],"isStart":false}),"instanceName":"1"});
            var sketch = newSketch(context, id + "F20", { "sketchPlane" : qUnion([Q0])});
            skLineSegment(sketch, "E83.bottom", {"start": v(0, 114.3) * mm, "end": v(203.2, 114.3) * mm, "construction": true});
            skLineSegment(sketch, "E83.top", {"start": v(0, -88.9) * mm, "end": v(203.2, -88.9) * mm, "construction": true});
            skLineSegment(sketch, "E83.left", {"start": v(0, 114.3) * mm, "end": v(0, -88.9) * mm, "construction": true});
            skLineSegment(sketch, "E83.right", {"start": v(203.2, 114.3) * mm, "end": v(203.2, -88.9) * mm, "construction": true});
            skLineSegment(sketch, "E84", {"start": v(101.6, 114.3) * mm, "end": v(101.6, -88.9) * mm, "construction": true});
            skLineSegment(sketch, "E85.bottom", {"start": v(177.8, 95.25) * mm, "end": v(25.4, 95.25) * mm});
            skLineSegment(sketch, "E85.top", {"start": v(177.8, -69.85) * mm, "end": v(25.4, -69.85) * mm});
            skLineSegment(sketch, "E85.left", {"start": v(184.15, 88.9) * mm, "end": v(184.15, -63.5) * mm});
            skLineSegment(sketch, "E85.right", {"start": v(19.05, 88.9) * mm, "end": v(19.05, -63.5) * mm});
            skPoint(sketch, "E85.middle", {"position": v(101.6, 12.7) * mm});
            skPoint(sketch, "E86.visualSharp", {"position": v(19.05, 95.25) * mm});
            skArc(sketch, "E86.filletArc", {"start": v(25.4, 95.25) * mm, "mid": v(20.9, 93.4) * mm, "end": v(19.05, 88.9) * mm});
            skPoint(sketch, "E87.visualSharp", {"position": v(184.15, 95.25) * mm});
            skArc(sketch, "E87.filletArc", {"start": v(184.15, 88.9) * mm, "mid": v(182.3, 93.4) * mm, "end": v(177.8, 95.25) * mm});
            skPoint(sketch, "E88.visualSharp", {"position": v(184.15, -69.85) * mm});
            skArc(sketch, "E88.filletArc", {"start": v(177.8, -69.85) * mm, "mid": v(182.3, -68) * mm, "end": v(184.15, -63.5) * mm});
            skPoint(sketch, "E89.visualSharp", {"position": v(19.05, -69.85) * mm});
            skArc(sketch, "E89.filletArc", {"start": v(19.05, -63.5) * mm, "mid": v(20.9, -68) * mm, "end": v(25.4, -69.85) * mm});
            skSolve(sketch);
        }
        {
            var Q0;
            Q0 = qSketchRegion(id + "F20", true);
            extrude(context, id + "F21", {"entities" : qUnion([Q0]), "operationType" : NewBodyOperationType.REMOVE, "endBound" : BoundingType.THROUGH_ALL, "oppositeDirection" : true, "depth" : 25.4 * mm});
        }
        {
            var Q0;
            Q0=makeQuery(id+"F12.opPattern","COPY",FACE,{"derivedFrom":makeQuery(id+"F8.opExtrude","CAP_FACE",FACE,{"disambiguationData":[OSD([sQuery(id+"F7.wireOp",EDGE,"E53.bottom"),sQuery(id+"F7.wireOp",EDGE,"E53.top"),sQuery(id+"F7.wireOp",EDGE,"E53.left"),sQuery(id+"F7.wireOp",EDGE,"E53.right")])],"isStart":true}),"instanceName":"1"});
            var sketch = newSketch(context, id + "F22", { "sketchPlane" : qUnion([Q0])});
            skArc(sketch, "E90.0", {"start": v(-12.7, 88.9) * mm, "mid": v(-16.42, 97.88) * mm, "end": v(-25.4, 101.6) * mm});
            skLineSegment(sketch, "E90.1", {"start": v(-12.7, -63.5) * mm, "end": v(-12.7, 88.9) * mm});
            skLineSegment(sketch, "E90.2", {"start": v(-25.4, 101.6) * mm, "end": v(-177.8, 101.6) * mm});
            skArc(sketch, "E90.3", {"start": v(-25.4, -76.2) * mm, "mid": v(-16.42, -72.48) * mm, "end": v(-12.7, -63.5) * mm});
            skArc(sketch, "E90.4", {"start": v(-177.8, 101.6) * mm, "mid": v(-186.78, 97.88) * mm, "end": v(-190.5, 88.9) * mm});
            skLineSegment(sketch, "E90.5", {"start": v(-190.5, -63.5) * mm, "end": v(-190.5, 88.9) * mm});
            skArc(sketch, "E90.6", {"start": v(-190.5, -63.5) * mm, "mid": v(-186.78, -72.48) * mm, "end": v(-177.8, -76.2) * mm});
            skLineSegment(sketch, "E90.7", {"start": v(-25.4, -76.2) * mm, "end": v(-177.8, -76.2) * mm});
            skLineSegment(sketch, "E91.0", {"start": v(-24.13, 92.71) * mm, "end": v(-168.9, 92.71) * mm});
            skLineSegment(sketch, "E91.1", {"start": v(-21.59, -64.77) * mm, "end": v(-21.59, 90.17) * mm});
            skLineSegment(sketch, "E91.2", {"start": v(-24.13, -67.3) * mm, "end": v(-168.9, -67.3) * mm});
            skLineSegment(sketch, "E91.3", {"start": v(-181.6, -54.6) * mm, "end": v(-181.6, 80.01) * mm});
            skArc(sketch, "E92", {"start": v(-177.8, 82.55) * mm, "mid": v(-173.3, 84.4) * mm, "end": v(-171.45, 88.9) * mm});
            skArc(sketch, "E93", {"start": v(-171.45, -63.5) * mm, "mid": v(-173.3, -59) * mm, "end": v(-177.8, -57.15) * mm});
            skLineSegment(sketch, "E94", {"start": v(-177.8, -57.15) * mm, "end": v(-179.07, -57.15) * mm});
            skLineSegment(sketch, "E95", {"start": v(-171.45, -63.5) * mm, "end": v(-171.45, -64.77) * mm});
            skLineSegment(sketch, "E96", {"start": v(-171.45, 88.9) * mm, "end": v(-171.45, 90.17) * mm});
            skLineSegment(sketch, "E97", {"start": v(-177.8, 82.55) * mm, "end": v(-179.07, 82.55) * mm});
            skPoint(sketch, "E98.visualSharp", {"position": v(-171.45, 92.71) * mm});
            skArc(sketch, "E98.filletArc", {"start": v(-168.9, 92.71) * mm, "mid": v(-170.7, 91.97) * mm, "end": v(-171.45, 90.17) * mm});
            skPoint(sketch, "E99.visualSharp", {"position": v(-181.6, 82.55) * mm});
            skArc(sketch, "E99.filletArc", {"start": v(-179.07, 82.55) * mm, "mid": v(-180.87, 81.8) * mm, "end": v(-181.6, 80.01) * mm});
            skPoint(sketch, "E100.visualSharp", {"position": v(-21.59, 92.71) * mm});
            skArc(sketch, "E100.filletArc", {"start": v(-21.59, 90.17) * mm, "mid": v(-22.33, 91.97) * mm, "end": v(-24.13, 92.71) * mm});
            skPoint(sketch, "E101.visualSharp", {"position": v(-171.45, -67.3) * mm});
            skArc(sketch, "E101.filletArc", {"start": v(-171.45, -64.77) * mm, "mid": v(-170.7, -66.57) * mm, "end": v(-168.9, -67.3) * mm});
            skPoint(sketch, "E102.visualSharp", {"position": v(-181.6, -57.15) * mm});
            skArc(sketch, "E102.filletArc", {"start": v(-181.6, -54.6) * mm, "mid": v(-180.87, -56.4) * mm, "end": v(-179.07, -57.15) * mm});
            skPoint(sketch, "E103.visualSharp", {"position": v(-21.59, -67.3) * mm});
            skArc(sketch, "E103.filletArc", {"start": v(-24.13, -67.3) * mm, "mid": v(-22.33, -66.57) * mm, "end": v(-21.59, -64.77) * mm});
            skSolve(sketch);
        }
        {
            var Q0;
            Q0 = qSketchRegion(id + "F22", true);
            extrude(context, id + "F23", {"entities" : qUnion([Q0]), "depth" : 3.17 * mm});
        }
        {
            var Q0;
            Q0=makeQuery(id+"F23.opExtrude","CAP_FACE",FACE,{"disambiguationData":[OSD([sQuery(id+"F22.wireOp",EDGE,"E90.0"),sQuery(id+"F22.wireOp",EDGE,"E90.1"),sQuery(id+"F22.wireOp",EDGE,"E90.2"),sQuery(id+"F22.wireOp",EDGE,"E90.3"),sQuery(id+"F22.wireOp",EDGE,"E90.4"),sQuery(id+"F22.wireOp",EDGE,"E90.5"),sQuery(id+"F22.wireOp",EDGE,"E90.6"),sQuery(id+"F22.wireOp",EDGE,"E90.7"),sQuery(id+"F22.wireOp",EDGE,"E91.0"),sQuery(id+"F22.wireOp",EDGE,"E91.1"),sQuery(id+"F22.wireOp",EDGE,"E91.2"),sQuery(id+"F22.wireOp",EDGE,"E91.3"),sQuery(id+"F22.wireOp",EDGE,"E92"),sQuery(id+"F22.wireOp",EDGE,"E93"),sQuery(id+"F22.wireOp",EDGE,"E94"),sQuery(id+"F22.wireOp",EDGE,"E95"),sQuery(id+"F22.wireOp",EDGE,"E96"),sQuery(id+"F22.wireOp",EDGE,"E97"),sQuery(id+"F22.wireOp",EDGE,"E98.filletArc"),sQuery(id+"F22.wireOp",EDGE,"E99.filletArc"),sQuery(id+"F22.wireOp",EDGE,"E100.filletArc"),sQuery(id+"F22.wireOp",EDGE,"E101.filletArc"),sQuery(id+"F22.wireOp",EDGE,"E102.filletArc"),sQuery(id+"F22.wireOp",EDGE,"E103.filletArc")])],"isStart":true});
            var sketch = newSketch(context, id + "F24", { "sketchPlane" : qUnion([Q0])});
            skCircle(sketch, "E104", {"center": v(177.8, 88.9) * mm, "radius": 3.18 * mm});
            skCircle(sketch, "E105", {"center": v(177.8, -63.5) * mm, "radius": 3.18 * mm});
            skSolve(sketch);
        }
        {
            var Q0;
            Q0 = qSketchRegion(id + "F24", true);
            var Q1;
            Q1=sQuery(id+"F24.wireOp",EDGE,"E104");
            extrude(context, id + "F25", {"entities" : qUnion([Q0]), "operationType" : NewBodyOperationType.REMOVE, "surfaceEntities" : qUnion([Q1]), "endBound" : BoundingType.THROUGH_ALL, "oppositeDirection" : true, "depth" : 25.4 * mm});
        }
        {
            var Q0;
            Q0=makeQuery(id+"F12.opPattern","COPY",FACE,{"derivedFrom":makeQuery(id+"F8.opExtrude","CAP_FACE",FACE,{"disambiguationData":[OSD([sQuery(id+"F7.wireOp",EDGE,"E53.bottom"),sQuery(id+"F7.wireOp",EDGE,"E53.top"),sQuery(id+"F7.wireOp",EDGE,"E53.left"),sQuery(id+"F7.wireOp",EDGE,"E53.right")])],"isStart":false}),"instanceName":"1"});
            var sketch = newSketch(context, id + "F26", { "sketchPlane" : qUnion([Q0])});
            skArc(sketch, "E106.0", {"start": v(184.15, 88.9) * mm, "mid": v(182.3, 93.4) * mm, "end": v(177.8, 95.25) * mm});
            skLineSegment(sketch, "E106.1", {"start": v(184.15, 88.9) * mm, "end": v(184.15, -63.5) * mm});
            skLineSegment(sketch, "E106.2", {"start": v(177.8, 95.25) * mm, "end": v(25.4, 95.25) * mm});
            skArc(sketch, "E106.3", {"start": v(177.8, -69.85) * mm, "mid": v(182.3, -68) * mm, "end": v(184.15, -63.5) * mm});
            skArc(sketch, "E106.4", {"start": v(25.4, 95.25) * mm, "mid": v(20.9, 93.4) * mm, "end": v(19.05, 88.9) * mm});
            skLineSegment(sketch, "E106.5", {"start": v(19.05, 88.9) * mm, "end": v(19.05, -63.5) * mm});
            skArc(sketch, "E106.6", {"start": v(19.05, -63.5) * mm, "mid": v(20.9, -68) * mm, "end": v(25.4, -69.85) * mm});
            skLineSegment(sketch, "E106.7", {"start": v(177.8, -69.85) * mm, "end": v(25.4, -69.85) * mm});
            skSolve(sketch);
        }
        {
            var Q0;
            Q0 = qSketchRegion(id + "F26", true);
            extrude(context, id + "F27", {"entities" : qUnion([Q0]), "oppositeDirection" : true, "depth" : (getVariable(context, 'thick')) * mm});
        }
        {
            var Q0;
            Q0=makeQuery(id+"F27.opExtrude","CAP_FACE",FACE,{"disambiguationData":[OSD([sQuery(id+"F26.wireOp",EDGE,"E106.0"),sQuery(id+"F26.wireOp",EDGE,"E106.1"),sQuery(id+"F26.wireOp",EDGE,"E106.2"),sQuery(id+"F26.wireOp",EDGE,"E106.3"),sQuery(id+"F26.wireOp",EDGE,"E106.4"),sQuery(id+"F26.wireOp",EDGE,"E106.5"),sQuery(id+"F26.wireOp",EDGE,"E106.6"),sQuery(id+"F26.wireOp",EDGE,"E106.7")])],"isStart":false});
            var sketch = newSketch(context, id + "F28", { "sketchPlane" : qUnion([Q0])});
            skCircle(sketch, "E107", {"center": v(-177.8, 88.9) * mm, "radius": 3.23 * mm});
            skCircle(sketch, "E108", {"center": v(-177.8, -63.5) * mm, "radius": 3.23 * mm});
            skLineSegment(sketch, "E109", {"start": v(-19.05, 12.7) * mm, "end": v(-184.15, 12.7) * mm, "construction": true});
            skCircle(sketch, "E110", {"center": v(-171.45, 12.7) * mm, "radius": 1.59 * mm});
            skSolve(sketch);
        }
        {
            var Q0;
            Q0 = qSketchRegion(id + "F28", true);
            extrude(context, id + "F29", {"entities" : qUnion([Q0]), "operationType" : NewBodyOperationType.REMOVE, "endBound" : BoundingType.THROUGH_ALL, "oppositeDirection" : true, "depth" : 25.4 * mm});
        }
        {
            var Q0;
            Q0=makeQuery(id+"F12.opPattern","COPY",FACE,{"derivedFrom":makeQuery(id+"F8.opExtrude","CAP_FACE",FACE,{"disambiguationData":[OSD([sQuery(id+"F7.wireOp",EDGE,"E53.bottom"),sQuery(id+"F7.wireOp",EDGE,"E53.top"),sQuery(id+"F7.wireOp",EDGE,"E53.left"),sQuery(id+"F7.wireOp",EDGE,"E53.right")])],"isStart":false}),"instanceName":"1"});
            var sketch = newSketch(context, id + "F30", { "sketchPlane" : qUnion([Q0])});
            skLineSegment(sketch, "E111.bottom", {"start": v(29.34, -108.2) * mm, "end": v(21.46, -108.2) * mm, "construction": true});
            skLineSegment(sketch, "E111.top", {"start": v(29.34, -95) * mm, "end": v(21.46, -95) * mm, "construction": true});
            skLineSegment(sketch, "E111.left", {"start": v(29.34, -108.2) * mm, "end": v(29.34, -95) * mm, "construction": true});
            skLineSegment(sketch, "E111.right", {"start": v(21.46, -108.2) * mm, "end": v(21.46, -95) * mm, "construction": true});
            skPoint(sketch, "E111.middle", {"position": v(25.4, -101.6) * mm});
            skCircle(sketch, "E112", {"center": v(25.4, -101.6) * mm, "radius": 3.18 * mm});
            skLineSegment(sketch, "E113", {"start": v(25.4, -101.6) * mm, "end": v(44.45, -101.6) * mm, "construction": true});
            skCircle(sketch, "E114", {"center": v(44.45, -101.6) * mm, "radius": 2.29 * mm});
            skSolve(sketch);
        }
        {
            var Q0;
            Q0 = qSketchRegion(id + "F30", true);
            extrude(context, id + "F31", {"entities" : qUnion([Q0]), "operationType" : NewBodyOperationType.REMOVE, "endBound" : BoundingType.THROUGH_ALL, "oppositeDirection" : true, "depth" : 25.4 * mm});
        }
        {
            var Q0;
            Q0=makeQuery(id+"F18.opExtrude","CAP_FACE",FACE,{"disambiguationData":[OSD([sQuery(id+"F17.wireOp",EDGE,"E82.bottom"),sQuery(id+"F17.wireOp",EDGE,"E82.top"),sQuery(id+"F17.wireOp",EDGE,"E82.left"),sQuery(id+"F17.wireOp",EDGE,"E82.right")])],"isStart":false});
            var sketch = newSketch(context, id + "F32", { "sketchPlane" : qUnion([Q0])});
            skCircle(sketch, "E115", {"center": v(12.7, 88.9) * mm, "radius": 3.18 * mm});
            skSolve(sketch);
        }
        {
            var Q0;
            Q0 = qSketchRegion(id + "F32", true);
            extrude(context, id + "F33", {"entities" : qUnion([Q0]), "operationType" : NewBodyOperationType.REMOVE, "endBound" : BoundingType.THROUGH_ALL, "oppositeDirection" : true, "depth" : 25.4 * mm});
        }
        {
            var Q0;
            Q0=makeQuery(id+"F8.opExtrude","CAP_FACE",FACE,{"disambiguationData":[OSD([sQuery(id+"F7.wireOp",EDGE,"E53.bottom"),sQuery(id+"F7.wireOp",EDGE,"E53.top"),sQuery(id+"F7.wireOp",EDGE,"E53.left"),sQuery(id+"F7.wireOp",EDGE,"E53.right")])],"isStart":true});
            var sketch = newSketch(context, id + "F34", { "sketchPlane" : qUnion([Q0])});
            skCircle(sketch, "E116", {"center": v(-25.4, -101.6) * mm, "radius": 3.94 * mm});
            skSolve(sketch);
        }
        {
            var Q0;
            Q0 = qSketchRegion(id + "F34", true);
            extrude(context, id + "F35", {"entities" : qUnion([Q0]), "operationType" : NewBodyOperationType.REMOVE, "endBound" : BoundingType.THROUGH_ALL, "oppositeDirection" : true, "depth" : 25.4 * mm});
        }
    });
